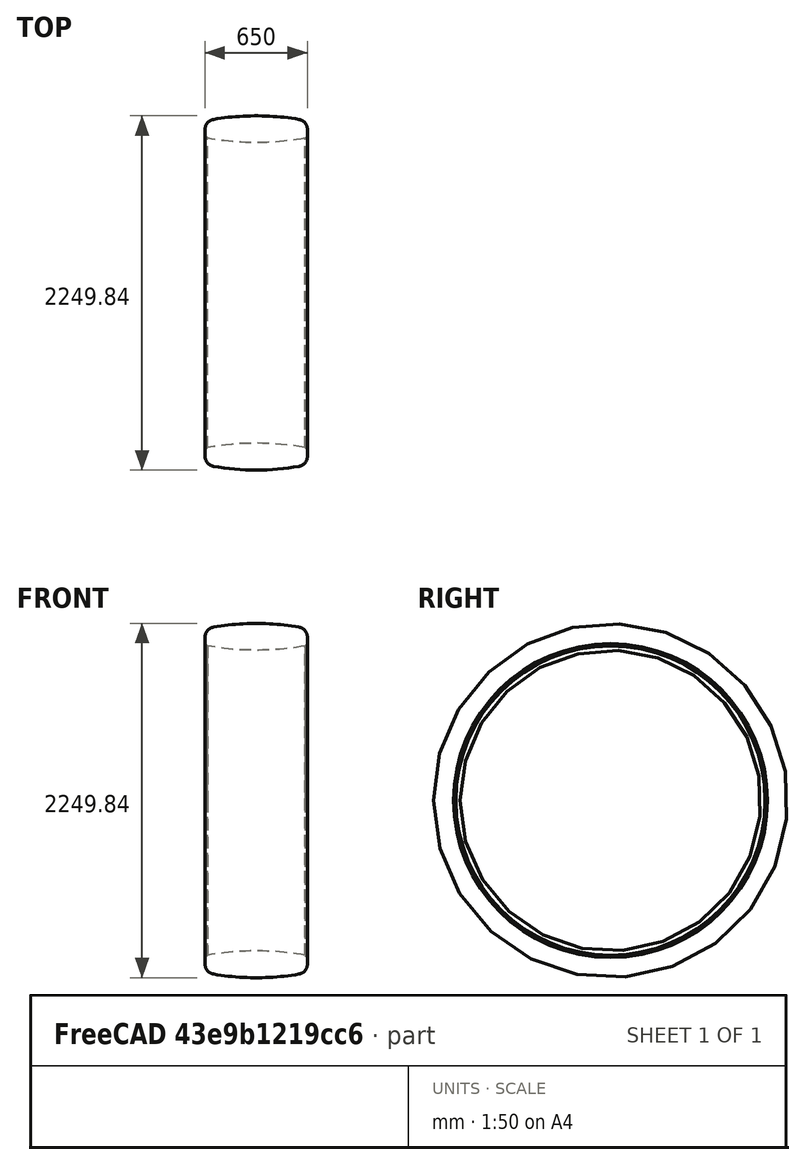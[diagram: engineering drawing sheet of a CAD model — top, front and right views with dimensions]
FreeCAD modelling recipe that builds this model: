
FCSTD DOCUMENT
Label: hacked_011
objects: Sketcher::SketchObject×1, PartDesign::Revolution×1
note: 3 computed .brp shape members not serialized (recipe doc carries the construction recipe); baked Part::Feature solids carry a one-line shape summary decoded from their .brp

FEATURE [Sketcher::SketchObject] Sketch
  sketch-geometry (10):
    g0: LineSegment [constr] StartX=-194.452 StartY=-954.92 StartZ=0 EndX=551.146 EndY=-954.92 EndZ=0
    g1: LineSegment StartX=0 StartY=-996.589 StartZ=0 EndX=0 EndY=-1038.76 EndZ=0
    g2: LineSegment StartX=650 StartY=-996.589 StartZ=0 EndX=650 EndY=-1038.76 EndZ=0
    g3: LineSegment [constr] StartX=-263.211 StartY=-1124.92 StartZ=0 EndX=396.606 EndY=-1124.92 EndZ=0
    g4: ArcOfCircle CenterX=586 CenterY=-1038.76 CenterZ=0 NormalX=0 NormalY=0 NormalZ=1 Radius=64 StartAngle=4.8818 EndAngle=6.28319
    g5: ArcOfCircle CenterX=64 CenterY=-1038.76 CenterZ=0 NormalX=0 NormalY=0 NormalZ=1 Radius=64 StartAngle=3.14159 EndAngle=4.54298
    g6: ArcOfCircle CenterX=325 CenterY=487.08 CenterZ=0 NormalX=0 NormalY=0 NormalZ=1 Radius=1612 StartAngle=4.54298 EndAngle=4.8818
    g7: ArcOfCircle CenterX=325 CenterY=-2723.92 CenterZ=0 NormalX=0 NormalY=0 NormalZ=1 Radius=1769 StartAngle=1.39415 EndAngle=1.74744
    g8: LineSegment StartX=635.858 StartY=-982.447 StartZ=0 EndX=650 EndY=-996.589 EndZ=0
    g9: LineSegment StartX=14.1421 StartY=-982.447 StartZ=0 EndX=0 EndY=-996.589 EndZ=0
  constraints (32):
    c: Horizontal(g0)
    c: DistanceY(g0) = -954.92
    c: Vertical(g1)
    c: Vertical(g2)
    c: DistanceX(g1) = 0
    c: DistanceX(g1,g2) = 650
    c: Horizontal(g3)
    c: DistanceY(g0,g3) = -170
    c: Radius(g4) = 64
    c: Radius(g5) = 64
    c: Tangent(g4,g2)
    c: Tangent(g1,g5)
    c: Tangent(g5,g6)
    c: Tangent(g6,g4)
    c: Tangent(g3,g6)
    c: Radius(g6) = 1612
    c: Radius(g7) = 1769
    c: Tangent(g0,g7)
    c: DistanceX(g6) = 325
    c: DistanceX(g7) = 325
    c: DistanceX(g3) = -263.211
    c: DistanceX(g0) = -194.452
    c: DistanceX(g0) = 551.146
    c: DistanceX(g3) = 396.606
    c: Coincident(g8,g7)
    c: Coincident(g9,g7)
    c: Coincident(g9,g1)
    c: Distance(g8) = 20
    c: Distance(g9) = 20
    c: Angle(g1,g9) = 2.35619
    c: Coincident(g8,g2)
    c: Angle(g8,g2) = 2.35619
FEATURE [PartDesign::Revolution] Revolution
  Angle = 360
  Axis = (1,0,0)
  Base = (0,0,0)
  ReferenceAxis = -> Sketch [H_Axis]
  Sketch = -> Sketch
